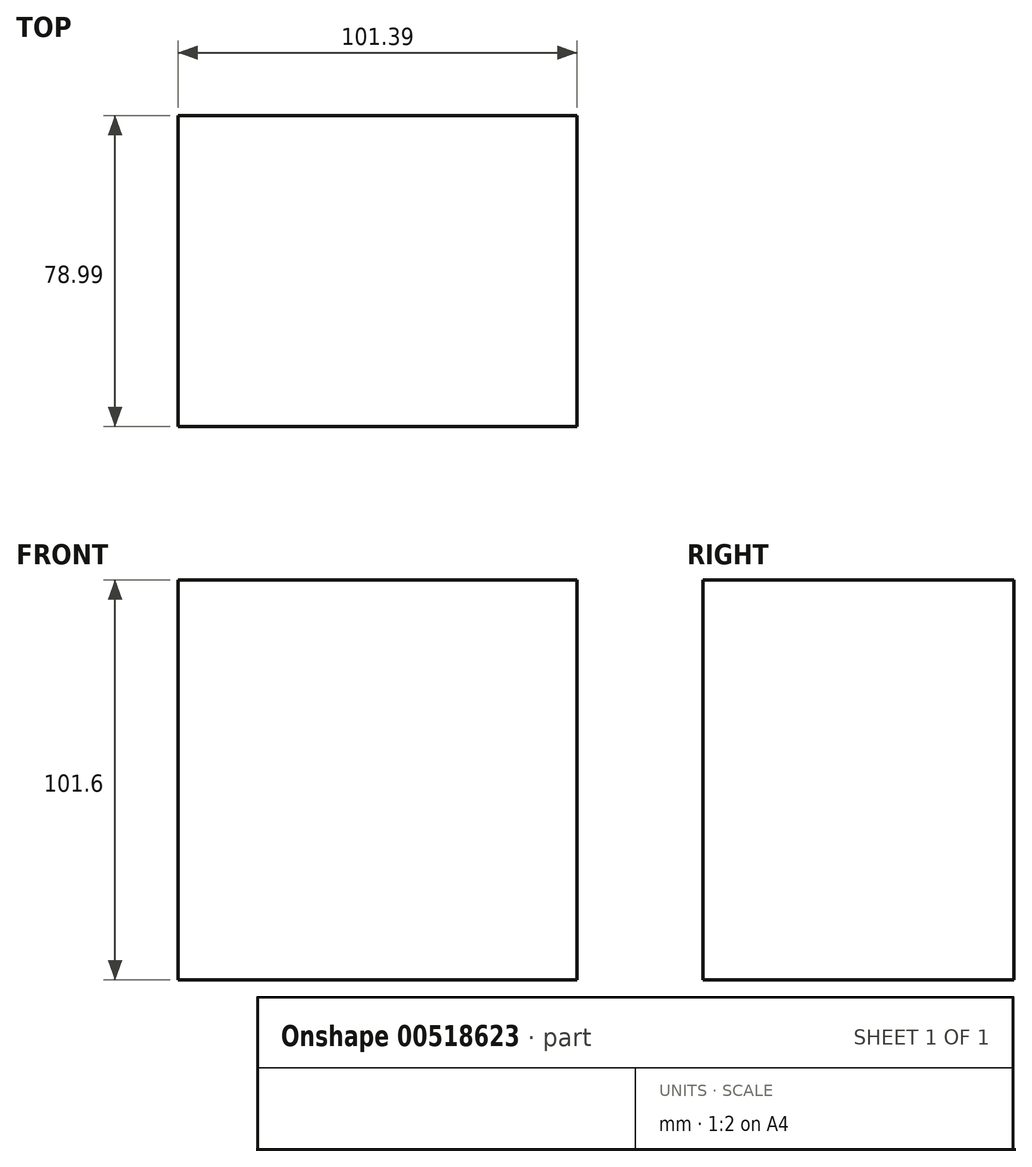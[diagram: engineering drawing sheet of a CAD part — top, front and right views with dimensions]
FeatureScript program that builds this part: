
annotation { "Feature Type Name" : "Feature", "Feature Type Description" : "" }
export const myFeature = defineFeature(function(context is Context, id is Id, definition is map)
    precondition{}
    {
        {
            var Q0;
            Q0=qCreatedBy(makeId("Top.planeOp"),FACE);
            var sketch = newSketch(context, id + "F0", { "sketchPlane" : qUnion([Q0])});
            skLineSegment(sketch, "E0", {"start": v(-53.12, 44.5) * mm, "end": v(48.27, 44.5) * mm});
            skLineSegment(sketch, "E1", {"start": v(48.27, 44.5) * mm, "end": v(48.27, -34.5) * mm});
            skLineSegment(sketch, "E2", {"start": v(48.27, -34.5) * mm, "end": v(-53.12, -34.5) * mm});
            skLineSegment(sketch, "E3", {"start": v(-53.12, -34.5) * mm, "end": v(-53.12, 44.5) * mm});
            skSolve(sketch);
        }
        {
            var Q0;
            Q0=makeQuery(id+"F0.imprint","IMPRINT",FACE,{"disambiguationData":[TD([[makeQuery(id+"F0.imprint","IMPRINT",EDGE,{"derivedFrom":sQuery(id+"F0.wireOp",EDGE,"E0")}),-1.0]])]});
            extrude(context, id + "F1", {"entities" : qUnion([Q0]), "depth" : 101.6 * mm, "offsetDistance" : 25.4 * mm});
        }
    });
